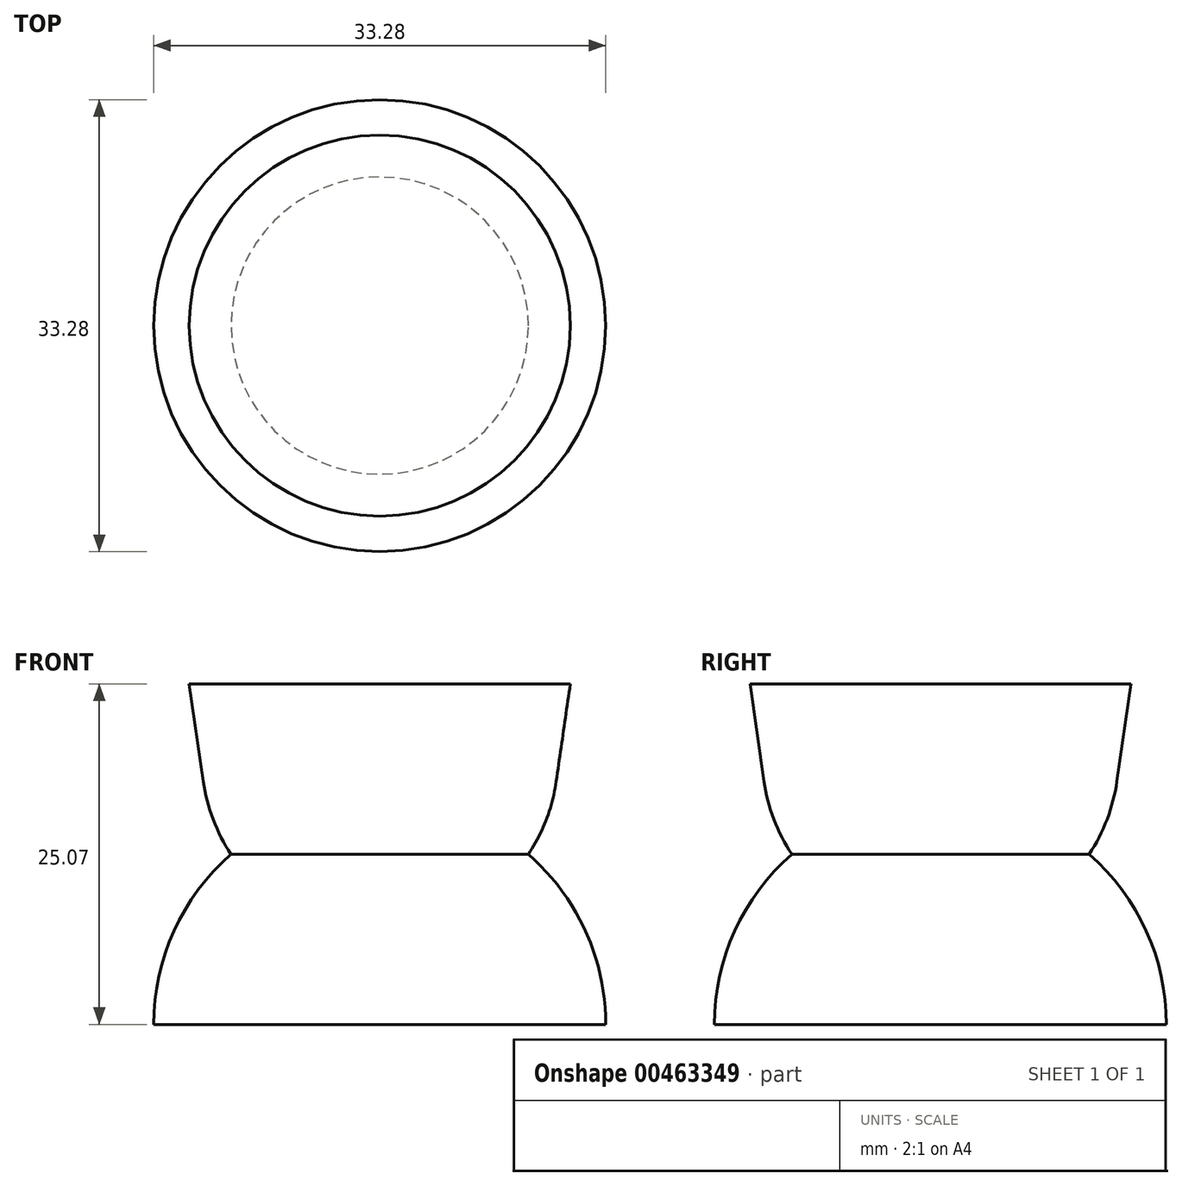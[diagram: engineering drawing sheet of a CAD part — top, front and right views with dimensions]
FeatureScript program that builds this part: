
annotation { "Feature Type Name" : "Feature", "Feature Type Description" : "" }
export const myFeature = defineFeature(function(context is Context, id is Id, definition is map)
    precondition{}
    {
        {
            var Q0;
            Q0=qCreatedBy(makeId("Front.planeOp"),FACE);
            var sketch = newSketch(context, id + "F0", { "sketchPlane" : qUnion([Q0])});
            skArc(sketch, "E0", {"start": v(16.64, 0) * mm, "mid": v(15.15, 6.88) * mm, "end": v(10.94, 12.53) * mm});
            skArc(sketch, "E1", {"start": v(10.94, 12.53) * mm, "mid": v(12.27, 15.1) * mm, "end": v(13, 17.9) * mm});
            skLineSegment(sketch, "E2", {"start": v(13, 17.9) * mm, "end": v(14.03, 25.07) * mm});
            skLineSegment(sketch, "E3", {"start": v(16.64, 0) * mm, "end": v(0, 0) * mm});
            skLineSegment(sketch, "E4", {"start": v(0, 25.07) * mm, "end": v(0, 0) * mm});
            skLineSegment(sketch, "E5", {"start": v(14.03, 25.07) * mm, "end": v(0, 25.07) * mm});
            skPoint(sketch, "E6.end.orphan", {"position": v(0, 31.94) * mm});
            skSolve(sketch);
        }
        {
            var Q0;
            Q0=qCreatedBy(makeId("Front.planeOp"),FACE);
            cPlane(context, id + "F1", {"entities" : qUnion([Q0]), "cplaneType" : CPlaneType.OFFSET, "offset" : 25 * mm, "width" : 150 * mm, "height" : 150 * mm});
        }
        {
            var Q0;
            Q0=makeQuery(id+"F0.imprint","IMPRINT",FACE,{"disambiguationData":[TD([[makeQuery(id+"F0.imprint","IMPRINT",EDGE,{"derivedFrom":sQuery(id+"F0.wireOp",EDGE,"E0")}),1.0]])]});
            var Q1;
            Q1=sQuery(id+"F0.wireOp",EDGE,"E4");
            revolve(context, id + "F2", {"entities" : qUnion([Q0]), "axis" : qUnion([Q1]), "revolveType" : RevolveType.FULL});
        }
    });
